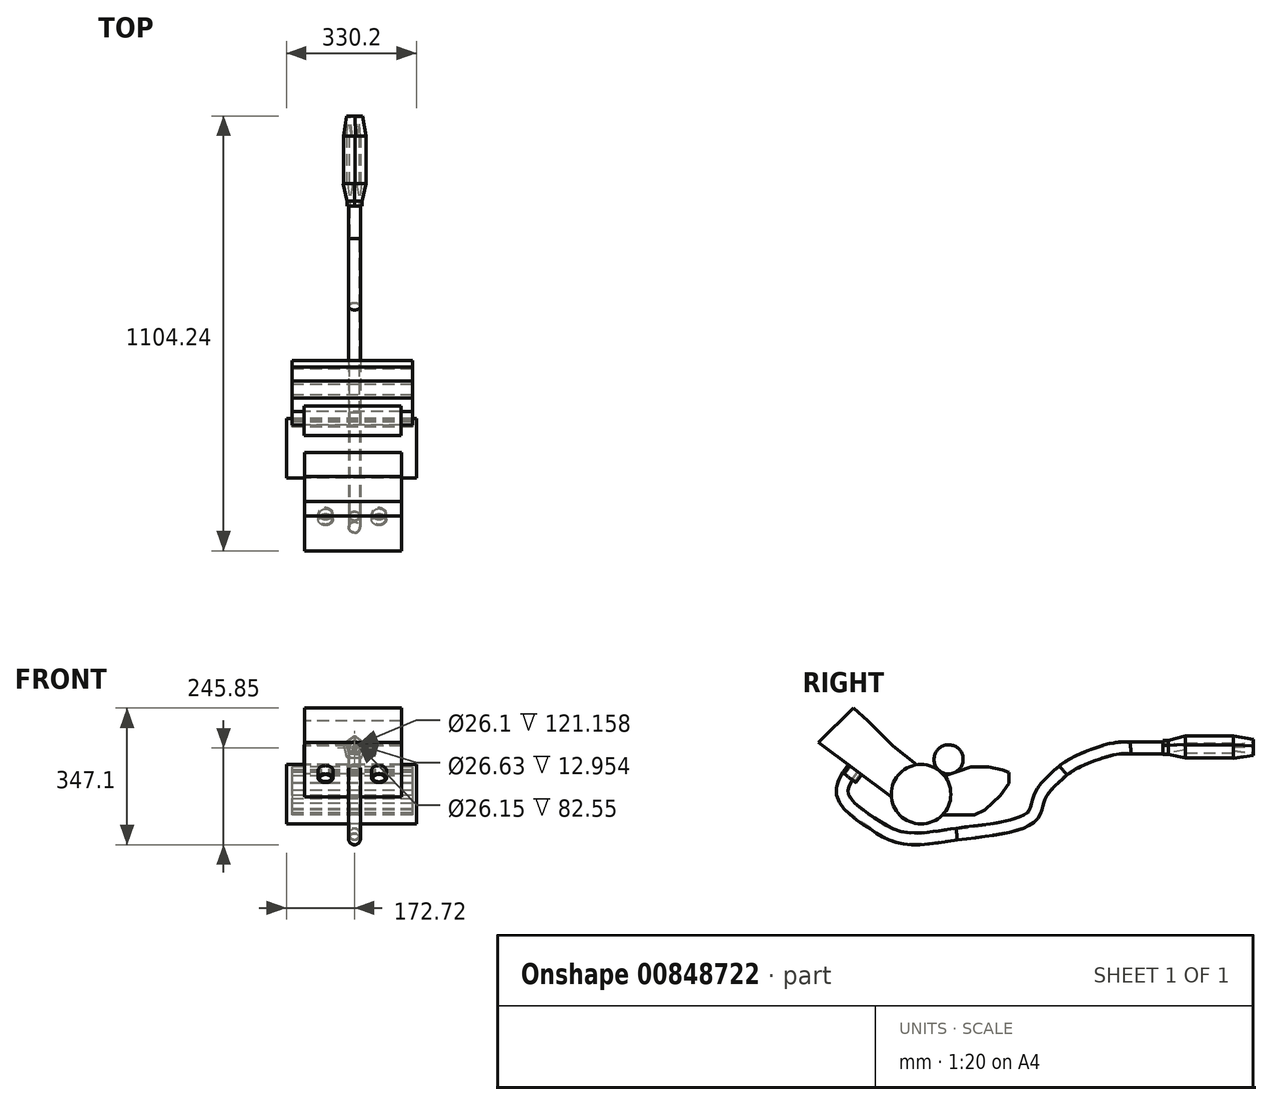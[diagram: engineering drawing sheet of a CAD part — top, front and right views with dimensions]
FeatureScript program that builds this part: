
annotation { "Feature Type Name" : "Feature", "Feature Type Description" : "" }
export const myFeature = defineFeature(function(context is Context, id is Id, definition is map)
    precondition{}
    {
        {
            var Q0;
            Q0=qCreatedBy(makeId("Front.planeOp"),FACE);
            var sketch = newSketch(context, id + "F0", { "sketchPlane" : qUnion([Q0])});
            skCircle(sketch, "E0.cCircle", {"center": v(0, 0) * mm, "radius": 24.63 * mm, "construction": true});
            skLineSegment(sketch, "E0.0", {"start": v(1.72, 30.4) * mm, "end": v(29.44, 7.76) * mm});
            skLineSegment(sketch, "E0.1", {"start": v(29.44, 7.76) * mm, "end": v(16.48, -25.6) * mm});
            skLineSegment(sketch, "E0.2", {"start": v(16.48, -25.6) * mm, "end": v(-19.26, -23.59) * mm});
            skLineSegment(sketch, "E0.3", {"start": v(-19.26, -23.59) * mm, "end": v(-28.38, 11.02) * mm});
            skLineSegment(sketch, "E0.4", {"start": v(-28.38, 11.02) * mm, "end": v(1.72, 30.4) * mm});
            skPoint(sketch, "E0.0.midPoint", {"position": v(15.58, 19.08) * mm});
            skCircle(sketch, "E1", {"center": v(0, 0) * mm, "radius": 13.05 * mm});
            skSolve(sketch);
        }
        {
            var Q0;
            Q0 = qSketchRegion(id + "F0", true);
            var Q1;
            Q1 = qSketchRegion(id + "F2", true);
            extrude(context, id + "F1", {"entities" : qUnion([Q0, Q1]), "depth" : 121.16 * mm, "offsetDistance" : 25.4 * mm});
        }
        {
            var Q0;
            Q0=qCreatedBy(makeId("Front.planeOp"),FACE);
            var sketch = newSketch(context, id + "F2", { "sketchPlane" : qUnion([Q0])});
            skSolve(sketch);
        }
        {
            var Q0;
            Q0=qCreatedBy(makeId("Front.planeOp"),FACE);
            cPlane(context, id + "F3", {"entities" : qUnion([Q0]), "cplaneType" : CPlaneType.OFFSET, "offset" : 50.8 * mm, "oppositeDirection" : true, "width" : 152.4 * mm, "height" : 152.4 * mm});
        }
        {
            var Q0;
            Q0=qCreatedBy(id+"F3.planeOp",FACE);
            var sketch = newSketch(context, id + "F4", { "sketchPlane" : qUnion([Q0])});
            skCircle(sketch, "E2.cCircle", {"center": v(0, 0) * mm, "radius": 21.53 * mm, "construction": true});
            skLineSegment(sketch, "E2.0", {"start": v(1.57, 21.48) * mm, "end": v(20.91, 5.15) * mm});
            skLineSegment(sketch, "E2.1", {"start": v(20.91, 5.15) * mm, "end": v(11.36, -18.3) * mm});
            skLineSegment(sketch, "E2.2", {"start": v(11.36, -18.3) * mm, "end": v(-13.9, -16.45) * mm});
            skLineSegment(sketch, "E2.3", {"start": v(-13.9, -16.45) * mm, "end": v(-19.94, 8.13) * mm});
            skLineSegment(sketch, "E2.4", {"start": v(-19.94, 8.13) * mm, "end": v(1.57, 21.48) * mm});
            skCircle(sketch, "E3.cCircle", {"center": v(0, 0) * mm, "radius": 13.66 * mm, "construction": true});
            skLineSegment(sketch, "E3.0", {"start": v(-15.37, 7) * mm, "end": v(1.91, 16.78) * mm});
            skLineSegment(sketch, "E3.1", {"start": v(1.91, 16.78) * mm, "end": v(16.55, 3.37) * mm});
            skLineSegment(sketch, "E3.2", {"start": v(16.55, 3.37) * mm, "end": v(8.32, -14.7) * mm});
            skLineSegment(sketch, "E3.3", {"start": v(8.32, -14.7) * mm, "end": v(-11.4, -12.45) * mm});
            skLineSegment(sketch, "E3.4", {"start": v(-11.4, -12.45) * mm, "end": v(-15.37, 7) * mm});
            skPoint(sketch, "E3.0.midPoint", {"position": v(-6.73, 11.9) * mm});
            skLineSegment(sketch, "E4", {"start": v(21.53, 0) * mm, "end": v(0, 0) * mm});
            skPoint(sketch, "E5.orphan", {"position": v(50.47, 0) * mm});
            skSolve(sketch);
        }
        {
            var Q0;
            Q0 = qSketchRegion(id + "F4", true);
            var Q1;
            Q1=makeQuery(id+"F1.opExtrude","CAP_VERTEX",VERTEX,{"disambiguationData":[OSD([sQuery(id+"F0.wireOp",EDGE,"E0.0"),sQuery(id+"F0.wireOp",EDGE,"E0.4")])],"isStart":true});
            extrude(context, id + "F5", {"entities" : qUnion([Q0]), "operationType" : NewBodyOperationType.ADD, "endBound" : BoundingType.UP_TO_VERTEX, "depth" : 50.8 * mm, "endBoundEntityVertex" : qUnion([Q1]), "offsetDistance" : 25.4 * mm, "hasDraft" : true, "draftAngle" : 8 * degree});
        }
        {
            var Q0;
            Q0=qCreatedBy(makeId("Front.planeOp"),FACE);
            cPlane(context, id + "F6", {"entities" : qUnion([Q0]), "cplaneType" : CPlaneType.OFFSET, "offset" : 165.35 * mm, "width" : 152.4 * mm, "height" : 152.4 * mm});
        }
        {
            var Q0;
            Q0=qCreatedBy(id+"F6.planeOp",FACE);
            var sketch = newSketch(context, id + "F7", { "sketchPlane" : qUnion([Q0])});
            skPoint(sketch, "E6.0.midPoint", {"position": v(9.47, 14.88) * mm});
            skPoint(sketch, "E7.orphan", {"position": v(3.3, 18.8) * mm});
            skPoint(sketch, "E6.1.start.orphan", {"position": v(15.64, 10.96) * mm});
            skCircle(sketch, "E8.cCircle", {"center": v(0, 0) * mm, "radius": 16.02 * mm, "construction": true});
            skLineSegment(sketch, "E8.0", {"start": v(0.08, 19.8) * mm, "end": v(18.86, 6.04) * mm});
            skLineSegment(sketch, "E8.1", {"start": v(18.86, 6.04) * mm, "end": v(11.57, -16.07) * mm});
            skLineSegment(sketch, "E8.2", {"start": v(11.57, -16.07) * mm, "end": v(-11.7, -15.97) * mm});
            skLineSegment(sketch, "E8.3", {"start": v(-11.7, -15.97) * mm, "end": v(-18.8, 6.2) * mm});
            skLineSegment(sketch, "E8.4", {"start": v(-18.8, 6.2) * mm, "end": v(0.08, 19.8) * mm});
            skPoint(sketch, "E8.0.midPoint", {"position": v(9.47, 12.92) * mm});
            skCircle(sketch, "E9", {"center": v(0, 0) * mm, "radius": 13.32 * mm});
            skSolve(sketch);
        }
        {
            var Q0;
            Q0 = qSketchRegion(id + "F7", true);
            extrude(context, id + "F8", {"entities" : qUnion([Q0]), "operationType" : NewBodyOperationType.ADD, "oppositeDirection" : true, "depth" : 44.2 * mm, "offsetDistance" : 25.4 * mm, "hasDraft" : true, "draftAngle" : 11 * degree, "hasSecondDirection" : true, "secondDirectionOppositeDirection" : false, "secondDirectionDepth" : 12.95 * mm});
        }
        {
            var Q0;
            Q0=qCreatedBy(makeId("Front.planeOp"),FACE);
            cPlane(context, id + "F9", {"entities" : qUnion([Q0]), "cplaneType" : CPlaneType.OFFSET, "offset" : 260.86 * mm, "width" : 152.4 * mm, "height" : 152.4 * mm});
        }
        {
            var Q0;
            Q0=qCreatedBy(id+"F9.planeOp",FACE);
            var sketch = newSketch(context, id + "F10", { "sketchPlane" : qUnion([Q0])});
            skCircle(sketch, "E10", {"center": v(0, 0) * mm, "radius": 15.18 * mm});
            skCircle(sketch, "E11", {"center": v(0, 0) * mm, "radius": 13.08 * mm});
            skSolve(sketch);
        }
        {
            var Q0;
            Q0 = qSketchRegion(id + "F10", true);
            extrude(context, id + "F11", {"entities" : qUnion([Q0]), "operationType" : NewBodyOperationType.ADD, "oppositeDirection" : true, "depth" : 82.55 * mm, "offsetDistance" : 25.4 * mm});
        }
        {
            var Q0;
            Q0=qCreatedBy(makeId("Right.planeOp"),FACE);
            var sketch = newSketch(context, id + "F12", { "sketchPlane" : qUnion([Q0])});
            skFitSpline(sketch, "E12", {"points": [v(-260.93, 0) * mm, v(-306.34, -2.74) * mm, v(-400.22, -36.6) * mm, v(-432.73, -57.2) * mm], "startDerivative": vector(-134.34, 5.96) * mm, "endDerivative": vector(-96.22, -71.55) * mm});
            skSolve(sketch);
        }
        {
            var Q0;
            Q0=makeQuery(id+"F11.opExtrude","CAP_FACE",FACE,{"disambiguationData":[OSD([sQuery(id+"F10.wireOp",EDGE,"E10"),sQuery(id+"F10.wireOp",EDGE,"E11")])],"isStart":true});
            var Q1;
            Q1=sQuery(id+"F12.wireOp",EDGE,"E12");
            sweep(context, id + "F13", {"operationType" : NewBodyOperationType.ADD, "profiles" : qUnion([Q0]), "path" : qUnion([Q1])});
        }
        {
            var Q0;
            Q0=qCreatedBy(makeId("Right.planeOp"),FACE);
            var sketch = newSketch(context, id + "F14", { "sketchPlane" : qUnion([Q0])});
            skFitSpline(sketch, "E13", {"points": [v(-432.48, -56.56) * mm, v(-493.45, -125.45) * mm, v(-511.4, -173.06) * mm, v(-702.56, -218.37) * mm], "startDerivative": vector(-247.64, -220.17) * mm, "endDerivative": vector(-545.41, -64.17) * mm});
            skSolve(sketch);
        }
        {
            var Q0;
            Q0=makeQuery(id+"F13.opSweep","CAP_FACE",FACE,{"disambiguationData":[OSD([sQuery(id+"F10.wireOp",EDGE,"E10"),sQuery(id+"F10.wireOp",EDGE,"E11"),sQuery(id+"F12.wireOp",VERTEX,"E12.end")])],"isStart":false});
            var Q1;
            Q1=sQuery(id+"F14.wireOp",EDGE,"E13");
            sweep(context, id + "F15", {"operationType" : NewBodyOperationType.ADD, "profiles" : qUnion([Q0]), "path" : qUnion([Q1])});
        }
        {
            var Q0;
            Q0=qCreatedBy(makeId("Right.planeOp"),FACE);
            var sketch = newSketch(context, id + "F16", { "sketchPlane" : qUnion([Q0])});
            skFitSpline(sketch, "E14", {"points": [v(-702.8, -217.33) * mm, v(-839.03, -227.16) * mm, v(-913.47, -192.05) * mm, v(-989.32, -124.63) * mm, v(-983.7, -81.09) * mm, v(-964.04, -51.6) * mm], "startDerivative": vector(-556.75, -88.42) * mm, "endDerivative": vector(150.31, 198.9) * mm});
            skSolve(sketch);
        }
        {
            var Q0;
            Q0=makeQuery(id+"F15.opSweep","CAP_FACE",FACE,{"disambiguationData":[OSD([sQuery(id+"F10.wireOp",EDGE,"E10"),sQuery(id+"F10.wireOp",EDGE,"E11"),sQuery(id+"F12.wireOp",VERTEX,"E12.end"),sQuery(id+"F14.wireOp",VERTEX,"E13.end")])],"isStart":false});
            var Q1;
            Q1=sQuery(id+"F16.wireOp",EDGE,"E14");
            sweep(context, id + "F17", {"operationType" : NewBodyOperationType.ADD, "profiles" : qUnion([Q0]), "path" : qUnion([Q1])});
        }
        {
            var Q0;
            Q0=qCreatedBy(makeId("Right.planeOp"),FACE);
            var sketch = newSketch(context, id + "F18", { "sketchPlane" : qUnion([Q0])});
            skLineSegment(sketch, "E15", {"start": v(-1053.44, 14.79) * mm, "end": v(-866, -125.95) * mm});
            skLineSegment(sketch, "E16", {"start": v(-866, -125.95) * mm, "end": v(-792.79, -50.85) * mm});
            skLineSegment(sketch, "E17", {"start": v(-792.79, -50.85) * mm, "end": v(-864.73, 5.95) * mm});
            skLineSegment(sketch, "E18", {"start": v(-864.73, 5.95) * mm, "end": v(-927.84, 68.43) * mm});
            skLineSegment(sketch, "E19", {"start": v(-1053.44, 14.79) * mm, "end": v(-965.08, 101.25) * mm});
            skLineSegment(sketch, "E20", {"start": v(-965.08, 101.25) * mm, "end": v(-927.84, 68.43) * mm});
            skSolve(sketch);
        }
        {
            var Q0;
            Q0 = qSketchRegion(id + "F18", true);
            extrude(context, id + "F19", {"entities" : qUnion([Q0]), "depth" : 119.38 * mm, "offsetDistance" : 25.4 * mm, "hasSecondDirection" : true, "secondDirectionOppositeDirection" : true, "secondDirectionDepth" : 127 * mm});
        }
        {
            var Q0;
            Q0=qCreatedBy(makeId("Right.planeOp"),FACE);
            var sketch = newSketch(context, id + "F20", { "sketchPlane" : qUnion([Q0])});
            skCircle(sketch, "E21", {"center": v(-793.18, -117.42) * mm, "radius": 75.53 * mm});
            skSolve(sketch);
        }
        {
            var Q0;
            Q0 = qSketchRegion(id + "F20", true);
            extrude(context, id + "F21", {"entities" : qUnion([Q0]), "operationType" : NewBodyOperationType.ADD, "depth" : 157.48 * mm, "offsetDistance" : 25.4 * mm, "hasSecondDirection" : true, "secondDirectionOppositeDirection" : true, "secondDirectionDepth" : 172.72 * mm});
        }
        {
            var Q0;
            Q0=qCreatedBy(makeId("Right.planeOp"),FACE);
            var sketch = newSketch(context, id + "F22", { "sketchPlane" : qUnion([Q0])});
            skCircle(sketch, "E22", {"center": v(-723.3, -28.85) * mm, "radius": 37.02 * mm});
            skSolve(sketch);
        }
        {
            var Q0;
            Q0=makeQuery(id+"F22.imprint","IMPRINT",FACE,{"disambiguationData":[TD([[makeQuery(id+"F22.imprint","IMPRINT",EDGE,{"derivedFrom":sQuery(id+"F22.wireOp",EDGE,"E22")}),1.0]])]});
            extrude(context, id + "F23", {"entities" : qUnion([Q0]), "depth" : 118.1 * mm, "offsetDistance" : 25.4 * mm, "hasSecondDirection" : true, "secondDirectionOppositeDirection" : true, "secondDirectionDepth" : 127.5 * mm});
        }
        {
            var Q0;
            Q0=qCreatedBy(makeId("Right.planeOp"),FACE);
            var sketch = newSketch(context, id + "F24", { "sketchPlane" : qUnion([Q0])});
            skLineSegment(sketch, "E23", {"start": v(-733.75, -70.46) * mm, "end": v(-723.5, -88.3) * mm});
            skLineSegment(sketch, "E24", {"start": v(-723.5, -88.3) * mm, "end": v(-718.29, -108.02) * mm});
            skLineSegment(sketch, "E25", {"start": v(-718.29, -108.02) * mm, "end": v(-718.29, -128.84) * mm});
            skLineSegment(sketch, "E26", {"start": v(-718.29, -128.84) * mm, "end": v(-721.37, -140.52) * mm});
            skLineSegment(sketch, "E27", {"start": v(-721.37, -140.52) * mm, "end": v(-726.67, -154.32) * mm});
            skLineSegment(sketch, "E28", {"start": v(-726.67, -154.32) * mm, "end": v(-734.9, -165.46) * mm});
            skLineSegment(sketch, "E29", {"start": v(-734.9, -165.46) * mm, "end": v(-739.41, -170.5) * mm});
            skLineSegment(sketch, "E30", {"start": v(-739.41, -170.5) * mm, "end": v(-657.98, -170.5) * mm});
            skLineSegment(sketch, "E31", {"start": v(-657.98, -170.5) * mm, "end": v(-630.77, -157.37) * mm});
            skLineSegment(sketch, "E32", {"start": v(-630.77, -157.37) * mm, "end": v(-591.37, -120.22) * mm});
            skLineSegment(sketch, "E33", {"start": v(-591.37, -120.22) * mm, "end": v(-569.98, -89.82) * mm});
            skLineSegment(sketch, "E34", {"start": v(-569.98, -89.82) * mm, "end": v(-569.98, -61.68) * mm});
            skLineSegment(sketch, "E35", {"start": v(-569.98, -61.68) * mm, "end": v(-586.5, -55.67) * mm});
            skLineSegment(sketch, "E36", {"start": v(-586.5, -55.67) * mm, "end": v(-622.52, -48.54) * mm});
            skLineSegment(sketch, "E37", {"start": v(-622.52, -48.54) * mm, "end": v(-666.05, -48.54) * mm});
            skLineSegment(sketch, "E38", {"start": v(-666.05, -48.54) * mm, "end": v(-700.15, -60.05) * mm});
            skLineSegment(sketch, "E39", {"start": v(-700.15, -60.05) * mm, "end": v(-733.75, -70.46) * mm});
            skSolve(sketch);
        }
        {
            var Q0;
            Q0 = qSketchRegion(id + "F24", true);
            extrude(context, id + "F25", {"entities" : qUnion([Q0]), "depth" : 147.32 * mm, "offsetDistance" : 25.4 * mm, "hasSecondDirection" : true, "secondDirectionOppositeDirection" : true, "secondDirectionDepth" : 158.5 * mm});
        }
        {
            var Q0;
            Q0=makeQuery(id+"F19.opExtrude","SWEPT_FACE",FACE,{"disambiguationData":[OSD([sQuery(id+"F18.wireOp",EDGE,"E15")])]});
            var sketch = newSketch(context, id + "F26", { "sketchPlane" : qUnion([Q0])});
            skCircle(sketch, "E40", {"center": v(62.3, 733.27) * mm, "radius": 18.8 * mm});
            skCircle(sketch, "E41", {"center": v(62.3, 733.27) * mm, "radius": 15.61 * mm});
            skCircle(sketch, "E42", {"center": v(-73.45, 733.27) * mm, "radius": 18.78 * mm});
            skCircle(sketch, "E43", {"center": v(-73.45, 733.27) * mm, "radius": 15.02 * mm});
            skSolve(sketch);
        }
        {
            var Q0;
            Q0 = qSketchRegion(id + "F26", true);
            extrude(context, id + "F27", {"entities" : qUnion([Q0]), "operationType" : NewBodyOperationType.ADD, "depth" : 25.4 * mm, "offsetDistance" : 25.4 * mm});
        }
    });
